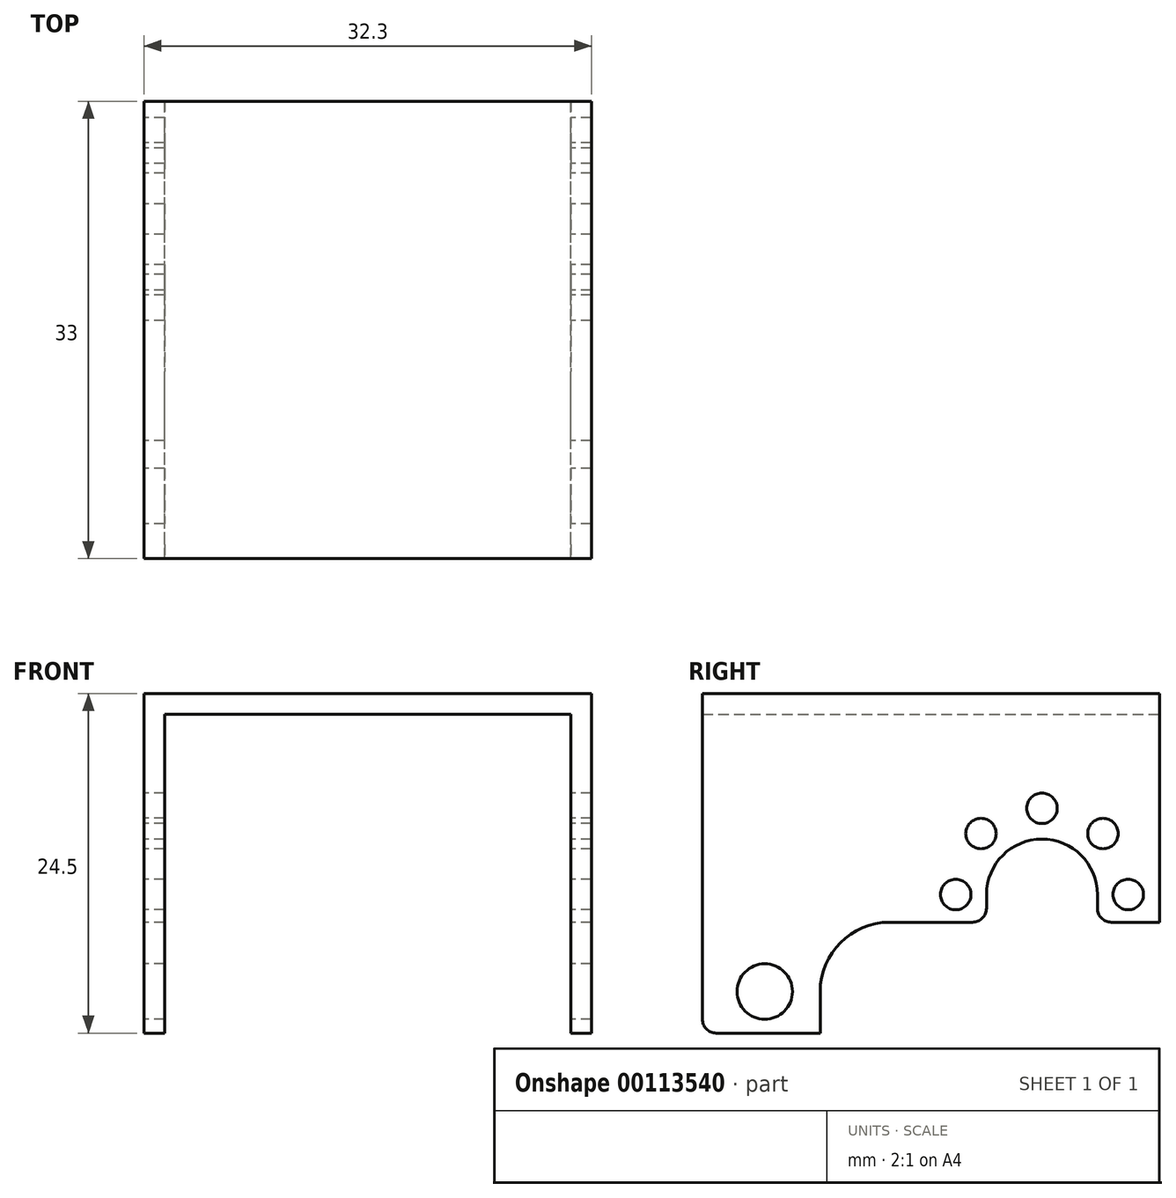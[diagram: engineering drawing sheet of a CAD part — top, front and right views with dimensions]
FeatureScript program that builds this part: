
annotation { "Feature Type Name" : "Feature", "Feature Type Description" : "" }
export const myFeature = defineFeature(function(context is Context, id is Id, definition is map)
    precondition{}
    {
        {
            var Q0;
            Q0=qCreatedBy(makeId("Front.planeOp"),FACE);
            var sketch = newSketch(context, id + "F0", { "sketchPlane" : qUnion([Q0])});
            skLineSegment(sketch, "E0.bottom", {"start": v(0, 0) * mm, "end": v(1.5, 0) * mm});
            skLineSegment(sketch, "E0.top", {"start": v(0, 24.5) * mm, "end": v(32.3, 24.5) * mm});
            skLineSegment(sketch, "E0.left", {"start": v(0, 0) * mm, "end": v(0, 24.5) * mm});
            skLineSegment(sketch, "E0.right", {"start": v(32.3, 0) * mm, "end": v(32.3, 24.5) * mm});
            skLineSegment(sketch, "E1.top", {"start": v(1.5, 23) * mm, "end": v(30.8, 23) * mm});
            skLineSegment(sketch, "E1.left", {"start": v(1.5, 0) * mm, "end": v(1.5, 23) * mm});
            skLineSegment(sketch, "E1.right", {"start": v(30.8, 0) * mm, "end": v(30.8, 23) * mm});
            skLineSegment(sketch, "E2.trimOffspring", {"start": v(30.8, 0) * mm, "end": v(32.3, 0) * mm});
            skSolve(sketch);
        }
        {
            var Q0;
            Q0=qSketchRegion(id+"F0",true);
            extrude(context, id + "F1", {"entities" : qUnion([Q0]), "depth" : 33 * mm});
        }
        {
            var Q0;
            Q0=makeQuery(id+"F1.opExtrude","SWEPT_FACE",FACE,{"disambiguationData":[OSD([sQuery(id+"F0.wireOp",EDGE,"E0.left")])]});
            var sketch = newSketch(context, id + "F2", { "sketchPlane" : qUnion([Q0])});
            skLineSegment(sketch, "E3.bottom", {"start": v(0, 0) * mm, "end": v(24.5, 0) * mm});
            skLineSegment(sketch, "E3.top", {"start": v(0, 8) * mm, "end": v(4.5, 8) * mm});
            skLineSegment(sketch, "E3.left", {"start": v(0, 0) * mm, "end": v(0, 8) * mm});
            skLineSegment(sketch, "E3.right", {"start": v(24.5, 0) * mm, "end": v(24.5, 8) * mm});
            skArc(sketch, "E4", {"start": v(12.5, 10) * mm, "mid": v(8.5, 14) * mm, "end": v(4.5, 10) * mm});
            skCircle(sketch, "E5", {"center": v(14.72, 10) * mm, "radius": 1.1 * mm});
            skCircle(sketch, "E6.1.0", {"center": v(12.9, 14.4) * mm, "radius": 1.1 * mm});
            skCircle(sketch, "E6.2.0", {"center": v(8.5, 16.22) * mm, "radius": 1.1 * mm});
            skCircle(sketch, "E6.3.0", {"center": v(4.1, 14.4) * mm, "radius": 1.1 * mm});
            skCircle(sketch, "E6.4.0", {"center": v(2.28, 10) * mm, "radius": 1.1 * mm});
            skLineSegment(sketch, "E7", {"start": v(4.5, 10) * mm, "end": v(4.5, 8) * mm});
            skLineSegment(sketch, "E8", {"start": v(12.5, 10) * mm, "end": v(12.5, 8) * mm});
            skLineSegment(sketch, "E9.trimOffspring", {"start": v(12.5, 8) * mm, "end": v(24.5, 8) * mm});
            skCircle(sketch, "E10", {"center": v(28.5, 3) * mm, "radius": 2 * mm});
            skSolve(sketch);
        }
        {
            var Q0;
            Q0=qSketchRegion(id+"F2",true);
            extrude(context, id + "F3", {"entities" : qUnion([Q0]), "operationType" : NewBodyOperationType.REMOVE, "endBound" : BoundingType.THROUGH_ALL, "oppositeDirection" : true, "depth" : 25 * mm});
        }
        {
            var Q0;
            Q0=makeQuery(id+"FhSWsQVfl24fQ8d_1.boolean.opBoolean","COPY",EDGE,{"disambiguationData":[OD(1.0)],"derivedFrom":makeQuery(id+"FhSWsQVfl24fQ8d_1.opExtrude","CAP_EDGE",EDGE,{"disambiguationData":[OSD([sQuery(id+"Fpe3hB4YBDp0oAt_1.wireOp",EDGE,"4bd2b07d-e855-4691-9f5c-57cf29639554.bottom")])],"isStart":false})});
            var Q1;
            Q1=makeQuery(id+"FhSWsQVfl24fQ8d_1.boolean.opBoolean","COPY",EDGE,{"disambiguationData":[OD(0.0)],"derivedFrom":makeQuery(id+"FhSWsQVfl24fQ8d_1.opExtrude","CAP_EDGE",EDGE,{"disambiguationData":[OSD([sQuery(id+"Fpe3hB4YBDp0oAt_1.wireOp",EDGE,"4bd2b07d-e855-4691-9f5c-57cf29639554.bottom")])],"isStart":false})});
            var Q2;
            Q2=makeQuery(id+"F3.boolean.opBoolean","COPY",EDGE,{"disambiguationData":[OD(0.0)],"derivedFrom":makeQuery(id+"F3.opExtrude","SWEPT_EDGE",EDGE,{"disambiguationData":[OSD([sQuery(id+"F2.wireOp",EDGE,"E3.top"),sQuery(id+"F2.wireOp",EDGE,"E7")])]})});
            var Q3;
            Q3=makeQuery(id+"F3.boolean.opBoolean","COPY",EDGE,{"disambiguationData":[OD(0.0)],"derivedFrom":makeQuery(id+"F3.opExtrude","SWEPT_EDGE",EDGE,{"disambiguationData":[OSD([sQuery(id+"F2.wireOp",EDGE,"E8"),sQuery(id+"F2.wireOp",EDGE,"E9.trimOffspring")])]})});
            var Q4;
            Q4=makeQuery(id+"F3.boolean.opBoolean","COPY",EDGE,{"disambiguationData":[OD(0.0)],"derivedFrom":makeQuery(id+"F3.opExtrude","SWEPT_EDGE",EDGE,{"disambiguationData":[OSD([sQuery(id+"F0.wireOp",EDGE,"E0.left"),sQuery(id+"F2.wireOp",EDGE,"E3.top"),sQuery(id+"F2.wireOp",EDGE,"E3.left")])]})});
            var Q5;
            Q5=makeQuery(id+"F3.boolean.opBoolean","COPY",EDGE,{"disambiguationData":[OD(0.0)],"derivedFrom":makeQuery(id+"F3.opExtrude","SWEPT_EDGE",EDGE,{"disambiguationData":[OSD([sQuery(id+"F0.wireOp",EDGE,"E0.bottom"),sQuery(id+"F0.wireOp",EDGE,"E0.left"),sQuery(id+"F2.wireOp",EDGE,"E3.bottom"),sQuery(id+"F2.wireOp",EDGE,"E3.right")])]})});
            var Q6;
            Q6=makeQuery(id+"F1.opExtrude","CAP_EDGE",EDGE,{"disambiguationData":[OSD([sQuery(id+"F0.wireOp",EDGE,"E0.bottom")])],"isStart":false});
            var Q7;
            Q7=makeQuery(id+"F1.opExtrude","CAP_EDGE",EDGE,{"disambiguationData":[OSD([sQuery(id+"F0.wireOp",EDGE,"E2.trimOffspring")])],"isStart":false});
            var Q8;
            Q8=makeQuery(id+"F3.boolean.opBoolean","COPY",EDGE,{"disambiguationData":[OD(1.0)],"derivedFrom":makeQuery(id+"F3.opExtrude","SWEPT_EDGE",EDGE,{"disambiguationData":[OSD([sQuery(id+"F0.wireOp",EDGE,"E0.bottom"),sQuery(id+"F0.wireOp",EDGE,"E0.left"),sQuery(id+"F2.wireOp",EDGE,"E3.bottom"),sQuery(id+"F2.wireOp",EDGE,"E3.right")])]})});
            var Q9;
            Q9=makeQuery(id+"F3.boolean.opBoolean","COPY",EDGE,{"disambiguationData":[OD(1.0)],"derivedFrom":makeQuery(id+"F3.opExtrude","SWEPT_EDGE",EDGE,{"disambiguationData":[OSD([sQuery(id+"F2.wireOp",EDGE,"E8"),sQuery(id+"F2.wireOp",EDGE,"E9.trimOffspring")])]})});
            var Q10;
            Q10=makeQuery(id+"F3.boolean.opBoolean","COPY",EDGE,{"disambiguationData":[OD(1.0)],"derivedFrom":makeQuery(id+"F3.opExtrude","SWEPT_EDGE",EDGE,{"disambiguationData":[OSD([sQuery(id+"F2.wireOp",EDGE,"E3.top"),sQuery(id+"F2.wireOp",EDGE,"E7")])]})});
            var Q11;
            Q11=makeQuery(id+"F3.boolean.opBoolean","COPY",EDGE,{"disambiguationData":[OD(1.0)],"derivedFrom":makeQuery(id+"F3.opExtrude","SWEPT_EDGE",EDGE,{"disambiguationData":[OSD([sQuery(id+"F0.wireOp",EDGE,"E0.left"),sQuery(id+"F2.wireOp",EDGE,"E3.top"),sQuery(id+"F2.wireOp",EDGE,"E3.left")])]})});
            fillet(context, id + "F4", {"entities" : qUnion([Q0, Q1, Q2, Q3, Q4, Q5, Q6, Q7, Q8, Q9, Q10, Q11]), "radius" : 1 * mm, "tangentPropagation" : true, "allowEdgeOverflow" : false});
        }
        {
            var Q0;
            Q0=makeQuery(id+"F3.boolean.opBoolean","COPY",EDGE,{"disambiguationData":[OD(1.0)],"derivedFrom":makeQuery(id+"F3.opExtrude","SWEPT_EDGE",EDGE,{"disambiguationData":[OSD([sQuery(id+"F2.wireOp",EDGE,"E3.right"),sQuery(id+"F2.wireOp",EDGE,"E9.trimOffspring")])]})});
            var Q1;
            Q1=makeQuery(id+"F3.boolean.opBoolean","COPY",EDGE,{"disambiguationData":[OD(0.0)],"derivedFrom":makeQuery(id+"F3.opExtrude","SWEPT_EDGE",EDGE,{"disambiguationData":[OSD([sQuery(id+"F2.wireOp",EDGE,"E3.right"),sQuery(id+"F2.wireOp",EDGE,"E9.trimOffspring")])]})});
            fillet(context, id + "F5", {"entities" : qUnion([Q0, Q1]), "radius" : 5 * mm, "tangentPropagation" : true, "allowEdgeOverflow" : false});
        }
    });
